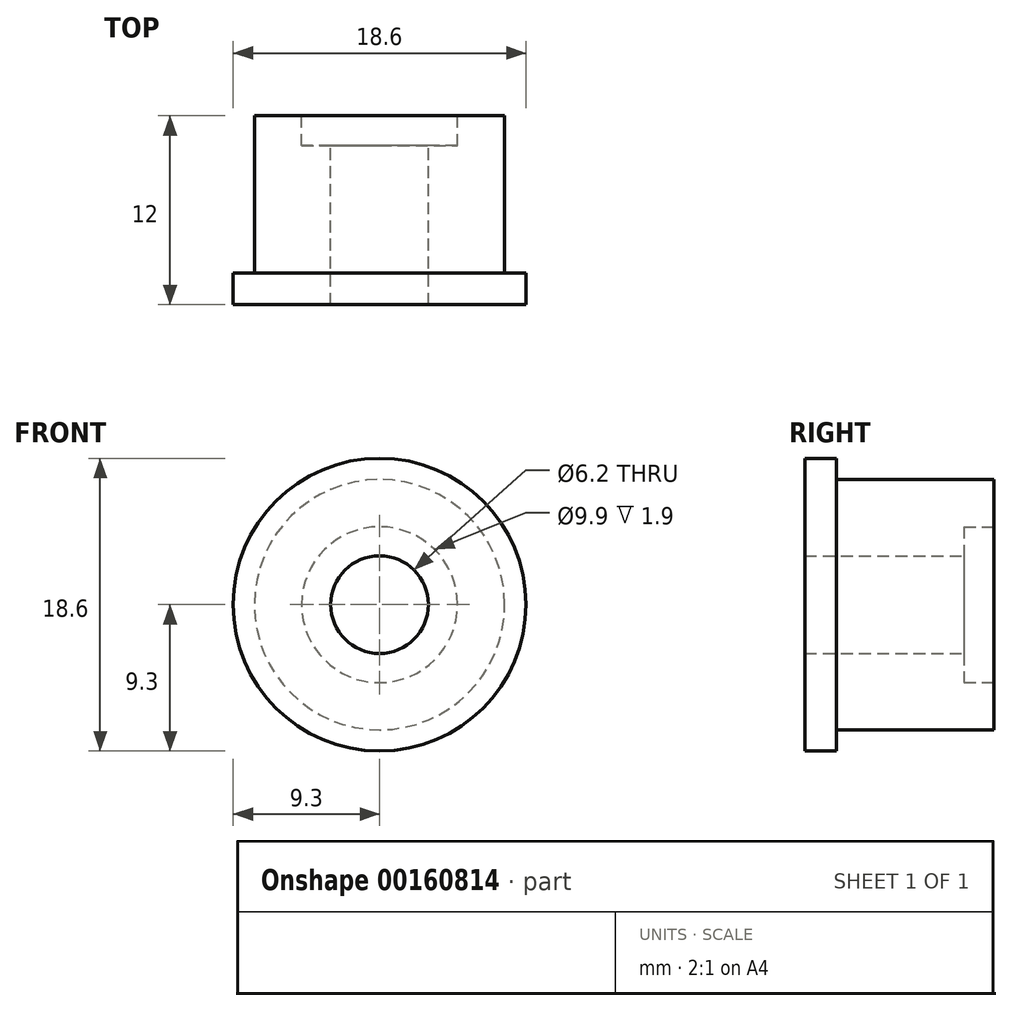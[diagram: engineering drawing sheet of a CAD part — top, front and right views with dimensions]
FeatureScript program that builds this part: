
annotation { "Feature Type Name" : "Feature", "Feature Type Description" : "" }
export const myFeature = defineFeature(function(context is Context, id is Id, definition is map)
    precondition{}
    {
        {
            var Q0;
            Q0=qCreatedBy(makeId("Right.planeOp"),FACE);
            var sketch = newSketch(context, id + "F0", { "sketchPlane" : qUnion([Q0])});
            skLineSegment(sketch, "E0", {"start": v(11.47, 0) * mm, "end": v(0, 0) * mm, "construction": true});
            skLineSegment(sketch, "E1", {"start": v(10.1, 3.1) * mm, "end": v(0, 3.1) * mm});
            skLineSegment(sketch, "E2", {"start": v(10.1, 3.1) * mm, "end": v(10.1, 4.95) * mm});
            skLineSegment(sketch, "E3", {"start": v(12, 4.95) * mm, "end": v(10.1, 4.95) * mm});
            skLineSegment(sketch, "E4", {"start": v(12, 4.95) * mm, "end": v(12, 7.95) * mm});
            skLineSegment(sketch, "E5", {"start": v(2, 7.95) * mm, "end": v(12, 7.95) * mm});
            skLineSegment(sketch, "E6", {"start": v(2, 7.95) * mm, "end": v(2, 9.3) * mm});
            skLineSegment(sketch, "E7", {"start": v(0, 9.3) * mm, "end": v(2, 9.3) * mm});
            skLineSegment(sketch, "E8", {"start": v(0, 9.3) * mm, "end": v(0, 3.1) * mm});
            skSolve(sketch);
        }
        {
            var Q0;
            Q0=makeQuery(id+"F0.imprint","IMPRINT",FACE,{"disambiguationData":[TD([[makeQuery(id+"F0.imprint","IMPRINT",EDGE,{"derivedFrom":sQuery(id+"F0.wireOp",EDGE,"E1")}),-1.0]])]});
            var Q1;
            Q1=sQuery(id+"F0.wireOp",EDGE,"E0");
            revolve(context, id + "F1", {"entities" : qUnion([Q0]), "axis" : qUnion([Q1]), "revolveType" : RevolveType.FULL});
        }
    });
